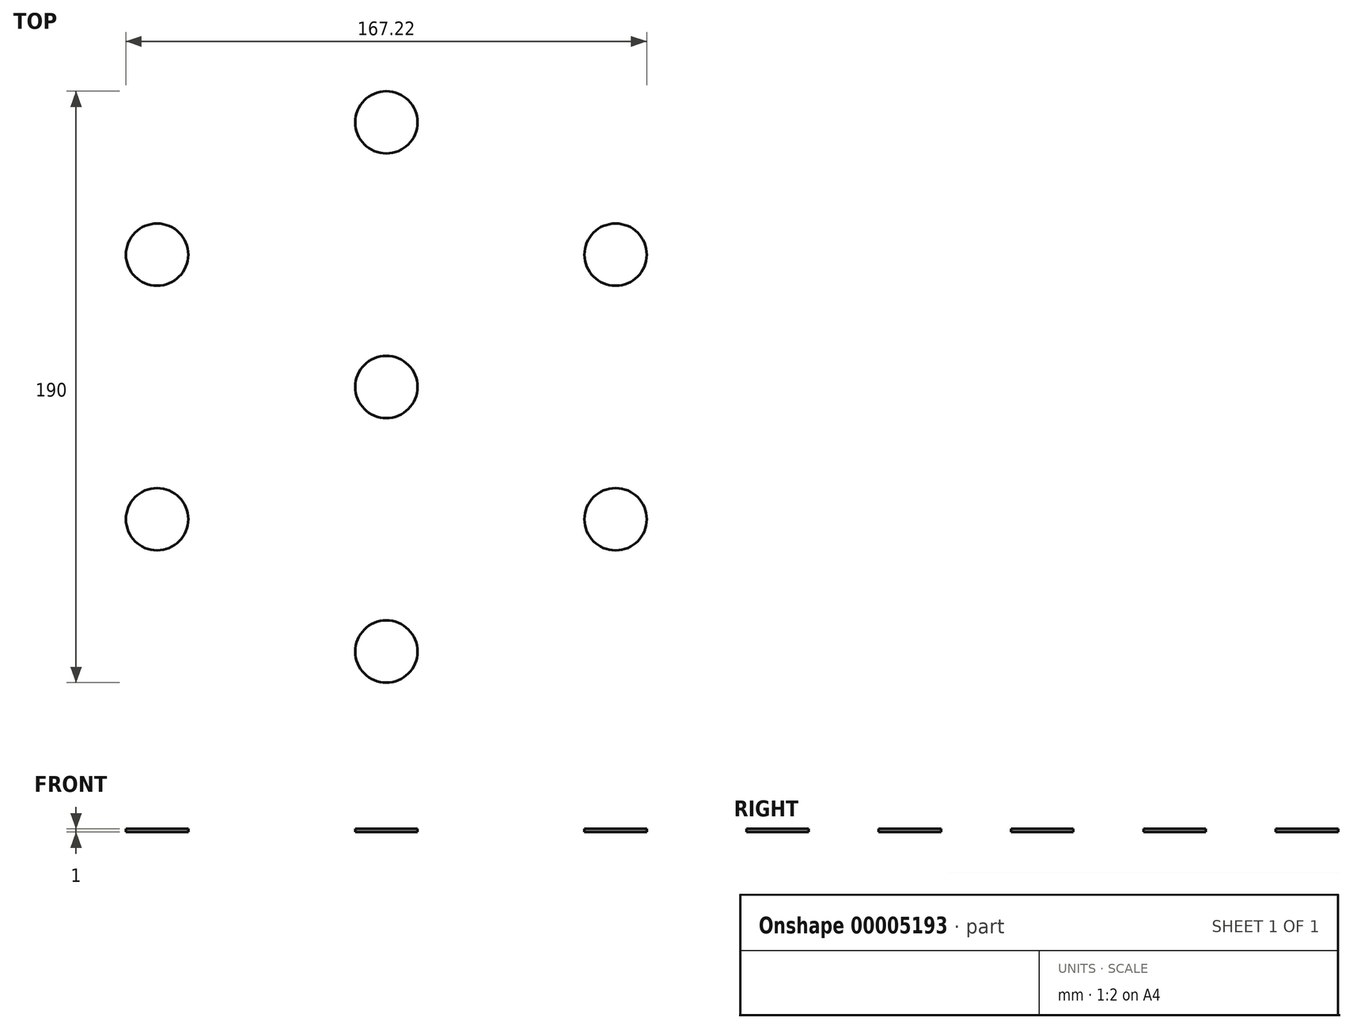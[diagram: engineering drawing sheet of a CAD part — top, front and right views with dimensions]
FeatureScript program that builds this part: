
annotation { "Feature Type Name" : "Feature", "Feature Type Description" : "" }
export const myFeature = defineFeature(function(context is Context, id is Id, definition is map)
    precondition{}
    {
        {
            var Q0;
            Q0=qCreatedBy(makeId("Top.planeOp"),FACE);
            var sketch = newSketch(context, id + "F0", { "sketchPlane" : qUnion([Q0])});
            skCircle(sketch, "E0", {"center": v(0, 0) * mm, "radius": 85 * mm, "construction": true});
            skLineSegment(sketch, "E1", {"start": v(0, 0) * mm, "end": v(0, 85) * mm, "construction": true});
            skCircle(sketch, "E2", {"center": v(0, 85) * mm, "radius": 10 * mm});
            skCircle(sketch, "E3.1.0", {"center": v(-73.61, 42.5) * mm, "radius": 10 * mm});
            skCircle(sketch, "E3.2.0", {"center": v(-73.61, -42.5) * mm, "radius": 10 * mm});
            skCircle(sketch, "E3.3.0", {"center": v(0, -85) * mm, "radius": 10 * mm});
            skCircle(sketch, "E3.4.0", {"center": v(73.61, -42.5) * mm, "radius": 10 * mm});
            skCircle(sketch, "E3.5.0", {"center": v(73.61, 42.5) * mm, "radius": 10 * mm});
            skCircle(sketch, "E4", {"center": v(0, 0) * mm, "radius": 10 * mm});
            skSolve(sketch);
        }
        {
            var Q0;
            Q0 = qSketchRegion(id + "F0", true);
            extrude(context, id + "F1", {"entities" : qUnion([Q0]), "depth" : 1 * mm});
        }
    });
